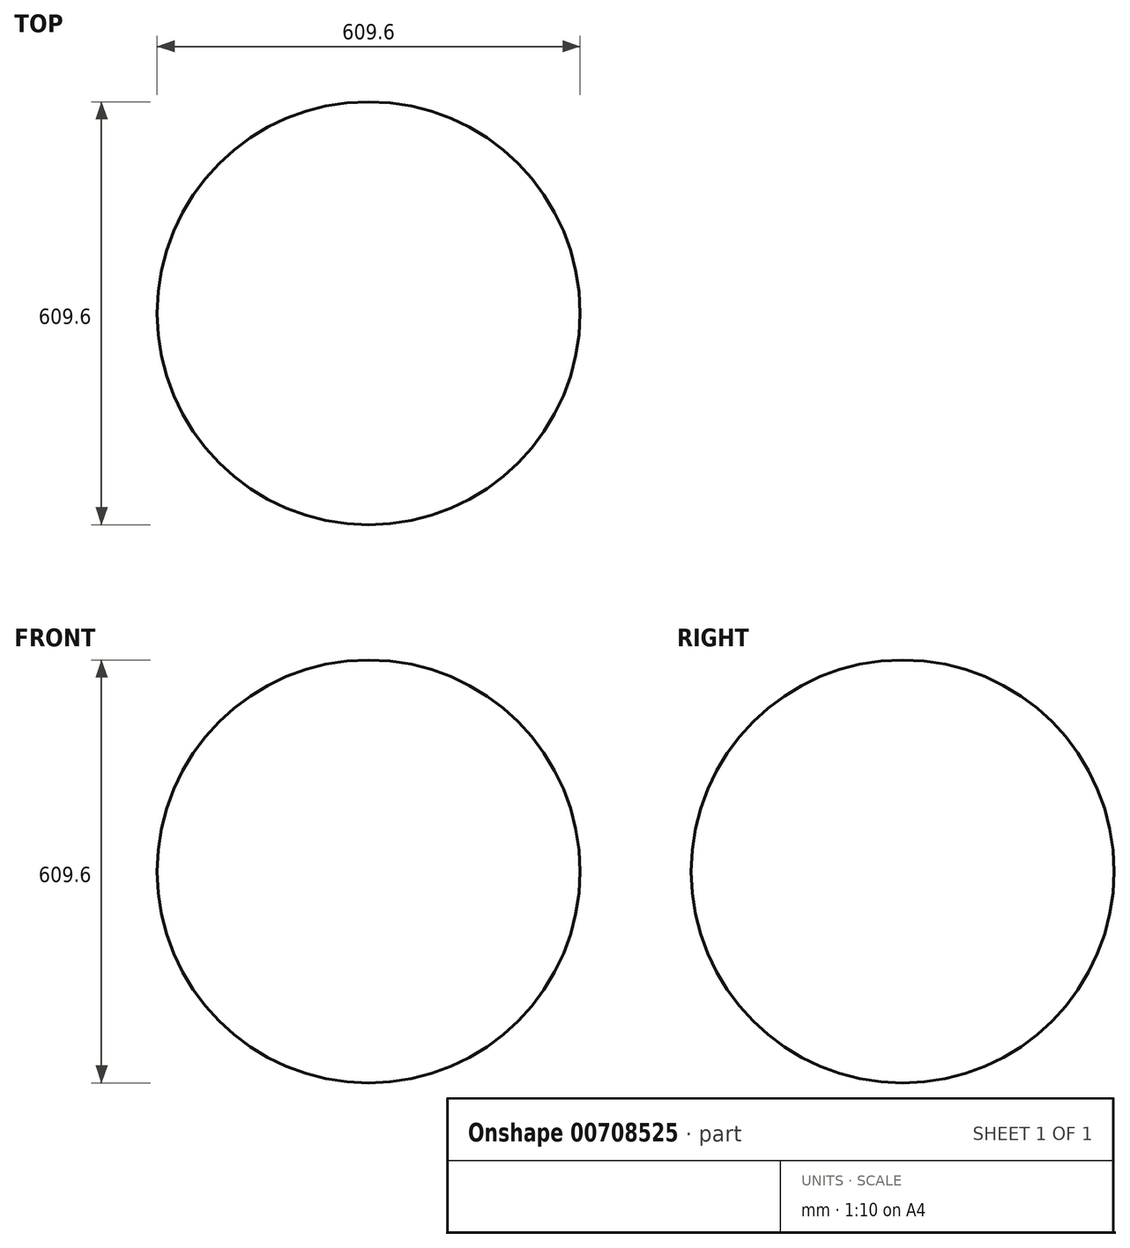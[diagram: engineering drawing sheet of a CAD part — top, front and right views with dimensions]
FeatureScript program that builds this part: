
annotation { "Feature Type Name" : "Feature", "Feature Type Description" : "" }
export const myFeature = defineFeature(function(context is Context, id is Id, definition is map)
    precondition{}
    {
        {
            var Q0;
            Q0=qCreatedBy(makeId("Front.planeOp"),FACE);
            var sketch = newSketch(context, id + "F0", { "sketchPlane" : qUnion([Q0])});
            skLineSegment(sketch, "E0", {"start": v(-304.8, 0) * mm, "end": v(304.8, 0) * mm});
            skArc(sketch, "E1", {"start": v(-304.8, 0) * mm, "mid": v(0, 304.8) * mm, "end": v(304.8, 0) * mm});
            skSolve(sketch);
        }
        {
            var Q0;
            Q0=makeQuery(id+"F0.imprint","IMPRINT",FACE,{"disambiguationData":[TD([[makeQuery(id+"F0.imprint","IMPRINT",EDGE,{"derivedFrom":sQuery(id+"F0.wireOp",EDGE,"E0")}),1.0]])]});
            var Q1;
            Q1=sQuery(id+"F0.wireOp",EDGE,"E0");
            revolve(context, id + "F1", {"surfaceOperationType" : NewSurfaceOperationType.NEW, "entities" : qUnion([Q0]), "axis" : qUnion([Q1]), "revolveType" : RevolveType.FULL});
        }
    });
